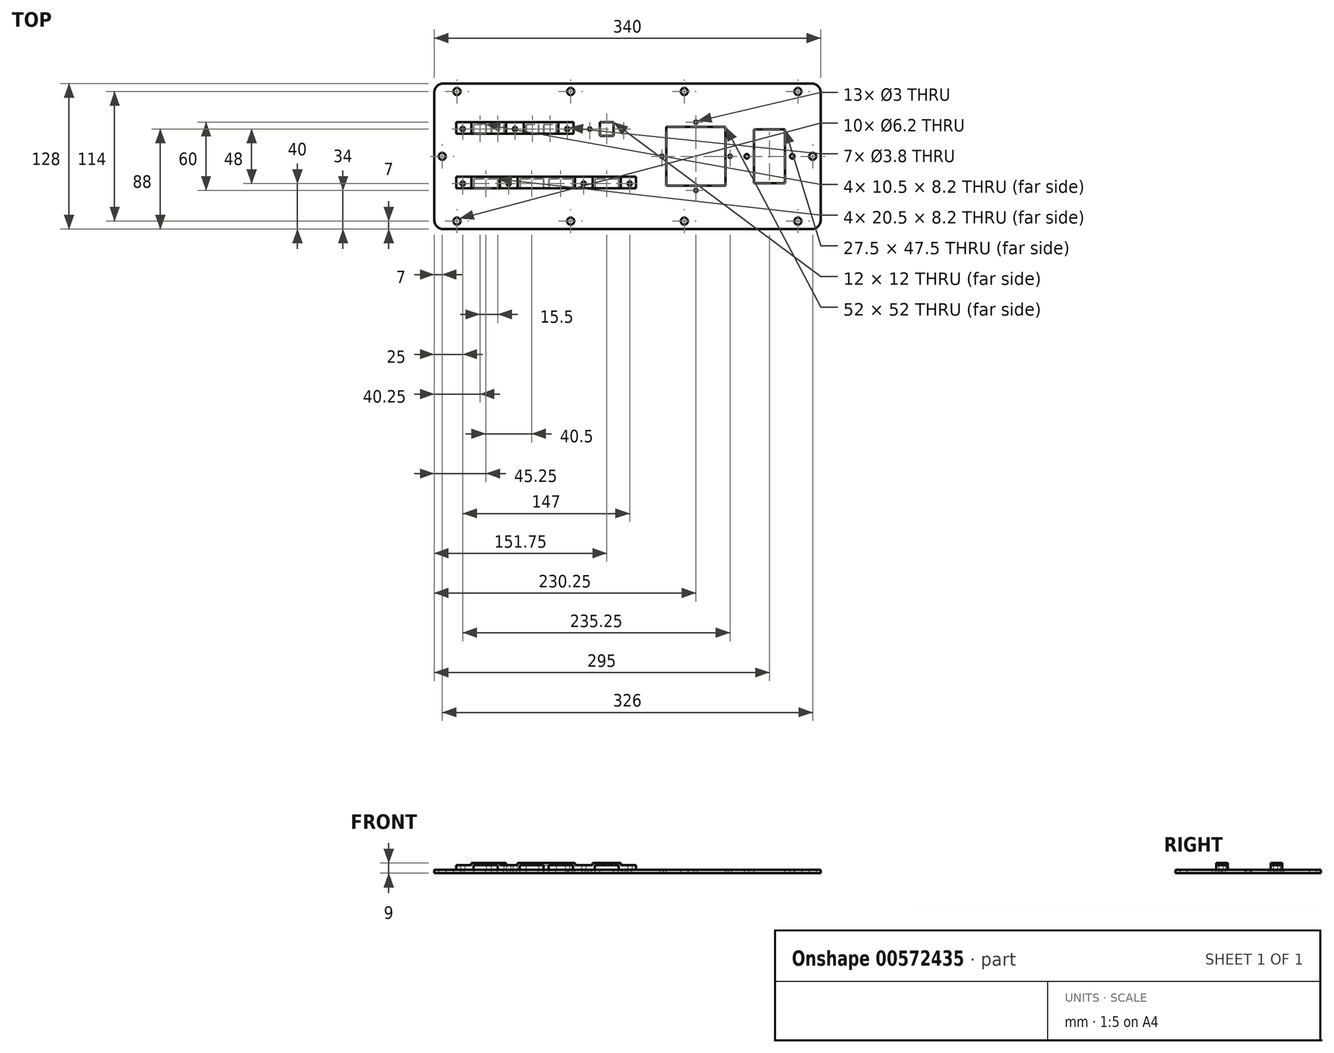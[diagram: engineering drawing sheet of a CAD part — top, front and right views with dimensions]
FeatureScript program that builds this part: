
annotation { "Feature Type Name" : "Feature", "Feature Type Description" : "" }
export const myFeature = defineFeature(function(context is Context, id is Id, definition is map)
    precondition{}
    {
        {
            var Q0;
            Q0=qCreatedBy(makeId("Top.planeOp"),FACE);
            var sketch = newSketch(context, id + "F0", { "sketchPlane" : qUnion([Q0])});
            skLineSegment(sketch, "E0.bottom", {"start": v(-170, 64) * mm, "end": v(170, 64) * mm});
            skLineSegment(sketch, "E0.top", {"start": v(-170, -64) * mm, "end": v(170, -64) * mm});
            skLineSegment(sketch, "E0.left", {"start": v(-170, 64) * mm, "end": v(-170, -64) * mm});
            skLineSegment(sketch, "E0.right", {"start": v(170, 64) * mm, "end": v(170, -64) * mm});
            skPoint(sketch, "E0.middle", {"position": v(0, 0) * mm});
            skLineSegment(sketch, "E1.0", {"start": v(-163, 57) * mm, "end": v(163, 57) * mm, "construction": true});
            skLineSegment(sketch, "E1.1", {"start": v(-163, 57) * mm, "end": v(-163, -57) * mm, "construction": true});
            skLineSegment(sketch, "E1.2", {"start": v(-163, -57) * mm, "end": v(163, -57) * mm, "construction": true});
            skLineSegment(sketch, "E1.3", {"start": v(163, 57) * mm, "end": v(163, -57) * mm, "construction": true});
            skCircle(sketch, "E2", {"center": v(-163, 0) * mm, "radius": 3.1 * mm});
            skCircle(sketch, "E3", {"center": v(-150, 57) * mm, "radius": 3.1 * mm});
            skCircle(sketch, "E4", {"center": v(-150, -57) * mm, "radius": 3.1 * mm});
            skCircle(sketch, "E5", {"center": v(-50, -57) * mm, "radius": 3.1 * mm});
            skCircle(sketch, "E6", {"center": v(-50, 57) * mm, "radius": 3.1 * mm});
            skLineSegment(sketch, "E7", {"start": v(0, 64) * mm, "end": v(0, -64) * mm, "construction": true});
            skCircle(sketch, "E8.MirrorC", {"center": v(50, -57) * mm, "radius": 3.1 * mm});
            skCircle(sketch, "E9.MirrorC", {"center": v(150, -57) * mm, "radius": 3.1 * mm});
            skCircle(sketch, "E10.MirrorC", {"center": v(163, 0) * mm, "radius": 3.1 * mm});
            skCircle(sketch, "E11.MirrorC", {"center": v(50, 57) * mm, "radius": 3.1 * mm});
            skCircle(sketch, "E12.MirrorC", {"center": v(150, 57) * mm, "radius": 3.1 * mm});
            skSolve(sketch);
        }
        {
            var Q0;
            Q0=makeQuery(id+"F0.imprint","IMPRINT",FACE,{"disambiguationData":[TD([[makeQuery(id+"F0.imprint","IMPRINT",EDGE,{"derivedFrom":sQuery(id+"F0.wireOp",EDGE,"E0.bottom")}),-1.0]])]});
            extrude(context, id + "F1", {"entities" : qUnion([Q0]), "depth" : 3 * mm, "offsetDistance" : 25 * mm});
        }
        {
            var Q0;
            Q0=makeQuery(id+"F1.opExtrude","CAP_FACE",FACE,{"disambiguationData":[OSD([sQuery(id+"F0.wireOp",EDGE,"E0.bottom"),sQuery(id+"F0.wireOp",EDGE,"E0.top"),sQuery(id+"F0.wireOp",EDGE,"E0.left"),sQuery(id+"F0.wireOp",EDGE,"E0.right"),sQuery(id+"F0.wireOp",EDGE,"E2"),sQuery(id+"F0.wireOp",EDGE,"E3"),sQuery(id+"F0.wireOp",EDGE,"E4"),sQuery(id+"F0.wireOp",EDGE,"E5"),sQuery(id+"F0.wireOp",EDGE,"E6"),sQuery(id+"F0.wireOp",EDGE,"E8.MirrorC"),sQuery(id+"F0.wireOp",EDGE,"E9.MirrorC"),sQuery(id+"F0.wireOp",EDGE,"E10.MirrorC"),sQuery(id+"F0.wireOp",EDGE,"E11.MirrorC"),sQuery(id+"F0.wireOp",EDGE,"E12.MirrorC")])],"isStart":false});
            var sketch = newSketch(context, id + "F2", { "sketchPlane" : qUnion([Q0])});
            skLineSegment(sketch, "E13.bottom", {"start": v(111.25, 23.75) * mm, "end": v(138.75, 23.75) * mm});
            skLineSegment(sketch, "E13.top", {"start": v(111.25, -23.75) * mm, "end": v(138.75, -23.75) * mm});
            skLineSegment(sketch, "E13.left", {"start": v(111.25, 23.75) * mm, "end": v(111.25, -23.75) * mm});
            skLineSegment(sketch, "E13.right", {"start": v(138.75, 23.75) * mm, "end": v(138.75, -23.75) * mm});
            skPoint(sketch, "E13.middle", {"position": v(125, 0) * mm});
            skLineSegment(sketch, "E14.bottom", {"start": v(34.25, 26) * mm, "end": v(86.25, 26) * mm});
            skLineSegment(sketch, "E14.top", {"start": v(34.25, -26) * mm, "end": v(86.25, -26) * mm});
            skLineSegment(sketch, "E14.left", {"start": v(34.25, 26) * mm, "end": v(34.25, -26) * mm});
            skLineSegment(sketch, "E14.right", {"start": v(86.25, 26) * mm, "end": v(86.25, -26) * mm});
            skPoint(sketch, "E14.middle", {"position": v(60.25, 0) * mm});
            skCircle(sketch, "E15", {"center": v(105, 0) * mm, "radius": 2 * mm});
            skPoint(sketch, "E15.centerSnap0", {"position": v(111.25, 0) * mm});
            skCircle(sketch, "E16", {"center": v(145, 0) * mm, "radius": 2 * mm});
            skPoint(sketch, "E16.centerSnap0", {"position": v(138.75, 0) * mm});
            skLineSegment(sketch, "E17", {"start": v(125, 23.75) * mm, "end": v(125, -23.75) * mm, "construction": true});
            skCircle(sketch, "E18", {"center": v(60.25, 30) * mm, "radius": 1.5 * mm});
            skCircle(sketch, "E19", {"center": v(60.25, -30) * mm, "radius": 1.5 * mm});
            skCircle(sketch, "E20", {"center": v(30.25, 0) * mm, "radius": 1.5 * mm});
            skCircle(sketch, "E21", {"center": v(90.25, 0) * mm, "radius": 1.5 * mm});
            skLineSegment(sketch, "E22", {"start": v(60.25, 26) * mm, "end": v(60.25, -26) * mm, "construction": true});
            skLineSegment(sketch, "E23", {"start": v(34.25, 0) * mm, "end": v(86.25, 0) * mm, "construction": true});
            skLineSegment(sketch, "E24.bottom", {"start": v(-135, -19.9) * mm, "end": v(-114.5, -19.9) * mm});
            skLineSegment(sketch, "E24.top", {"start": v(-135, -28.1) * mm, "end": v(-114.5, -28.1) * mm});
            skLineSegment(sketch, "E24.left", {"start": v(-135, -19.9) * mm, "end": v(-135, -28.1) * mm});
            skLineSegment(sketch, "E24.right", {"start": v(-114.5, -19.9) * mm, "end": v(-114.5, -28.1) * mm});
            skPoint(sketch, "E24.middle", {"position": v(-124.75, -24) * mm});
            skLineSegment(sketch, "E25.bottom", {"start": v(-94.5, -19.9) * mm, "end": v(-74, -19.9) * mm});
            skLineSegment(sketch, "E25.top", {"start": v(-94.5, -28.1) * mm, "end": v(-74, -28.1) * mm});
            skLineSegment(sketch, "E25.left", {"start": v(-94.5, -19.9) * mm, "end": v(-94.5, -28.1) * mm});
            skLineSegment(sketch, "E25.right", {"start": v(-74, -19.9) * mm, "end": v(-74, -28.1) * mm});
            skPoint(sketch, "E25.middle", {"position": v(-84.25, -24) * mm});
            skPoint(sketch, "E25.middle.positionSnap0", {"position": v(-114.5, -24) * mm});
            skPoint(sketch, "E25.centerSnap0", {"position": v(-114.5, -24) * mm});
            skLineSegment(sketch, "E26.bottom", {"start": v(-69, -19.9) * mm, "end": v(-48.5, -19.9) * mm});
            skLineSegment(sketch, "E26.top", {"start": v(-69, -28.1) * mm, "end": v(-48.5, -28.1) * mm});
            skLineSegment(sketch, "E26.left", {"start": v(-69, -19.9) * mm, "end": v(-69, -28.1) * mm});
            skLineSegment(sketch, "E26.right", {"start": v(-48.5, -19.9) * mm, "end": v(-48.5, -28.1) * mm});
            skPoint(sketch, "E26.middle", {"position": v(-58.75, -24) * mm});
            skLineSegment(sketch, "E27.bottom", {"start": v(-28.5, -19.9) * mm, "end": v(-8, -19.9) * mm});
            skLineSegment(sketch, "E27.top", {"start": v(-28.5, -28.1) * mm, "end": v(-8, -28.1) * mm});
            skLineSegment(sketch, "E27.left", {"start": v(-28.5, -19.9) * mm, "end": v(-28.5, -28.1) * mm});
            skLineSegment(sketch, "E27.right", {"start": v(-8, -19.9) * mm, "end": v(-8, -28.1) * mm});
            skPoint(sketch, "E27.middle", {"position": v(-18.25, -24) * mm});
            skCircle(sketch, "E28", {"center": v(-104.5, -24) * mm, "radius": 1.5 * mm});
            skPoint(sketch, "E28.centerSnap0", {"position": v(-94.5, -24) * mm});
            skCircle(sketch, "E29", {"center": v(-38.5, -24) * mm, "radius": 1.5 * mm});
            skPoint(sketch, "E29.centerSnap0", {"position": v(-48.5, -24) * mm});
            skCircle(sketch, "E30", {"center": v(2, -24) * mm, "radius": 1.5 * mm});
            skCircle(sketch, "E31", {"center": v(-145, -24) * mm, "radius": 1.5 * mm});
            skLineSegment(sketch, "E32.bottom", {"start": v(-124.5, 19.9) * mm, "end": v(-135, 19.9) * mm});
            skLineSegment(sketch, "E32.top", {"start": v(-124.5, 28.1) * mm, "end": v(-135, 28.1) * mm});
            skLineSegment(sketch, "E32.left", {"start": v(-124.5, 19.9) * mm, "end": v(-124.5, 28.1) * mm});
            skLineSegment(sketch, "E32.right", {"start": v(-135, 19.9) * mm, "end": v(-135, 28.1) * mm});
            skPoint(sketch, "E32.middle", {"position": v(-129.75, 24) * mm});
            skLineSegment(sketch, "E33.bottom", {"start": v(-119.5, 28.1) * mm, "end": v(-109, 28.1) * mm});
            skLineSegment(sketch, "E33.top", {"start": v(-119.5, 19.9) * mm, "end": v(-109, 19.9) * mm});
            skLineSegment(sketch, "E33.left", {"start": v(-119.5, 28.1) * mm, "end": v(-119.5, 19.9) * mm});
            skLineSegment(sketch, "E33.right", {"start": v(-109, 28.1) * mm, "end": v(-109, 19.9) * mm});
            skPoint(sketch, "E33.middle", {"position": v(-114.25, 24) * mm});
            skLineSegment(sketch, "E34.bottom", {"start": v(-89, 28.1) * mm, "end": v(-78.5, 28.1) * mm});
            skLineSegment(sketch, "E34.top", {"start": v(-89, 19.9) * mm, "end": v(-78.5, 19.9) * mm});
            skLineSegment(sketch, "E34.left", {"start": v(-89, 28.1) * mm, "end": v(-89, 19.9) * mm});
            skLineSegment(sketch, "E34.right", {"start": v(-78.5, 28.1) * mm, "end": v(-78.5, 19.9) * mm});
            skPoint(sketch, "E34.middle", {"position": v(-83.75, 24) * mm});
            skPoint(sketch, "E34.middle.positionSnap0", {"position": v(-109, 24) * mm});
            skPoint(sketch, "E34.centerSnap0", {"position": v(-109, 24) * mm});
            skLineSegment(sketch, "E35.bottom", {"start": v(-73.5, 28.1) * mm, "end": v(-63, 28.1) * mm});
            skLineSegment(sketch, "E35.top", {"start": v(-73.5, 19.9) * mm, "end": v(-63, 19.9) * mm});
            skLineSegment(sketch, "E35.left", {"start": v(-73.5, 28.1) * mm, "end": v(-73.5, 19.9) * mm});
            skLineSegment(sketch, "E35.right", {"start": v(-63, 28.1) * mm, "end": v(-63, 19.9) * mm});
            skPoint(sketch, "E35.middle", {"position": v(-68.25, 24) * mm});
            skCircle(sketch, "E36", {"center": v(-145, 24) * mm, "radius": 1.5 * mm});
            skPoint(sketch, "E36.centerSnap0", {"position": v(-135, 24) * mm});
            skCircle(sketch, "E37", {"center": v(-99, 24) * mm, "radius": 1.5 * mm});
            skPoint(sketch, "E37.centerSnap0", {"position": v(-124.5, 24) * mm});
            skCircle(sketch, "E38", {"center": v(-53, 24) * mm, "radius": 1.5 * mm});
            skPoint(sketch, "E38.centerSnap0", {"position": v(-63, 24) * mm});
            skLineSegment(sketch, "E39.bottom", {"start": v(-24.25, 30) * mm, "end": v(-12.25, 30) * mm});
            skLineSegment(sketch, "E39.top", {"start": v(-24.25, 18) * mm, "end": v(-12.25, 18) * mm});
            skLineSegment(sketch, "E39.left", {"start": v(-24.25, 30) * mm, "end": v(-24.25, 18) * mm});
            skLineSegment(sketch, "E39.right", {"start": v(-12.25, 30) * mm, "end": v(-12.25, 18) * mm});
            skPoint(sketch, "E39.middle", {"position": v(-18.25, 24) * mm});
            skCircle(sketch, "E40", {"center": v(-33.25, 24) * mm, "radius": 1.5 * mm});
            skPoint(sketch, "E40.centerSnap0", {"position": v(-24.25, 24) * mm});
            skCircle(sketch, "E41", {"center": v(-3.25, 24) * mm, "radius": 1.5 * mm});
            skPoint(sketch, "E41.centerSnap0", {"position": v(-12.25, 24) * mm});
            skLineSegment(sketch, "E42", {"start": v(-18.25, 30) * mm, "end": v(-18.25, 18) * mm, "construction": true});
            skSolve(sketch);
        }
        {
            var Q0;
            Q0 = qSketchRegion(id + "F2", true);
            extrude(context, id + "F3", {"entities" : qUnion([Q0]), "operationType" : NewBodyOperationType.REMOVE, "endBound" : BoundingType.THROUGH_ALL, "oppositeDirection" : true, "depth" : 25 * mm, "offsetDistance" : 25 * mm});
        }
        {
            var Q0;
            Q0=makeQuery(id+"F1.opExtrude","SWEPT_EDGE",EDGE,{"disambiguationData":[OSD([sQuery(id+"F0.wireOp",EDGE,"E0.top"),sQuery(id+"F0.wireOp",EDGE,"E0.right")])]});
            var Q1;
            Q1=makeQuery(id+"F1.opExtrude","SWEPT_EDGE",EDGE,{"disambiguationData":[OSD([sQuery(id+"F0.wireOp",EDGE,"E0.bottom"),sQuery(id+"F0.wireOp",EDGE,"E0.right")])]});
            var Q2;
            Q2=makeQuery(id+"F1.opExtrude","SWEPT_EDGE",EDGE,{"disambiguationData":[OSD([sQuery(id+"F0.wireOp",EDGE,"E0.top"),sQuery(id+"F0.wireOp",EDGE,"E0.left")])]});
            var Q3;
            Q3=makeQuery(id+"F1.opExtrude","SWEPT_EDGE",EDGE,{"disambiguationData":[OSD([sQuery(id+"F0.wireOp",EDGE,"E0.bottom"),sQuery(id+"F0.wireOp",EDGE,"E0.left")])]});
            fillet(context, id + "F4", {"entities" : qUnion([Q0, Q1, Q2, Q3]), "radius" : 8 * mm, "tangentPropagation" : true, "allowEdgeOverflow" : false});
        }
        {
            var Q0;
            Q0=makeQuery(id+"F1.opExtrude","CAP_FACE",FACE,{"disambiguationData":[OSD([sQuery(id+"F0.wireOp",EDGE,"E0.bottom"),sQuery(id+"F0.wireOp",EDGE,"E0.top"),sQuery(id+"F0.wireOp",EDGE,"E0.left"),sQuery(id+"F0.wireOp",EDGE,"E0.right"),sQuery(id+"F0.wireOp",EDGE,"E2"),sQuery(id+"F0.wireOp",EDGE,"E3"),sQuery(id+"F0.wireOp",EDGE,"E4"),sQuery(id+"F0.wireOp",EDGE,"E5"),sQuery(id+"F0.wireOp",EDGE,"E6"),sQuery(id+"F0.wireOp",EDGE,"E8.MirrorC"),sQuery(id+"F0.wireOp",EDGE,"E9.MirrorC"),sQuery(id+"F0.wireOp",EDGE,"E10.MirrorC"),sQuery(id+"F0.wireOp",EDGE,"E11.MirrorC"),sQuery(id+"F0.wireOp",EDGE,"E12.MirrorC")])],"isStart":false});
            var sketch = newSketch(context, id + "F5", { "sketchPlane" : qUnion([Q0])});
            skLineSegment(sketch, "E43.0", {"start": v(111.25, -23.75) * mm, "end": v(138.75, -23.75) * mm});
            skLineSegment(sketch, "E44.0", {"start": v(-162, 64) * mm, "end": v(162, 64) * mm});
            skLineSegment(sketch, "E44.1", {"start": v(-162, -64) * mm, "end": v(162, -64) * mm});
            skLineSegment(sketch, "E44.2", {"start": v(-170, 56) * mm, "end": v(-170, -56) * mm});
            skLineSegment(sketch, "E44.3", {"start": v(170, 56) * mm, "end": v(170, -56) * mm});
            skArc(sketch, "E45.0", {"start": v(170, 56) * mm, "mid": v(167.66, 61.66) * mm, "end": v(162, 64) * mm});
            skArc(sketch, "E45.1", {"start": v(-162, 64) * mm, "mid": v(-167.66, 61.66) * mm, "end": v(-170, 56) * mm});
            skArc(sketch, "E45.2", {"start": v(-170, -56) * mm, "mid": v(-167.66, -61.66) * mm, "end": v(-162, -64) * mm});
            skArc(sketch, "E45.3", {"start": v(162, -64) * mm, "mid": v(167.66, -61.66) * mm, "end": v(170, -56) * mm});
            skLineSegment(sketch, "E46.0", {"start": v(138.75, 23.75) * mm, "end": v(138.75, -23.75) * mm});
            skLineSegment(sketch, "E46.1", {"start": v(111.25, 23.75) * mm, "end": v(138.75, 23.75) * mm});
            skLineSegment(sketch, "E46.2", {"start": v(111.25, 23.75) * mm, "end": v(111.25, -23.75) * mm});
            skLineSegment(sketch, "E46.3", {"start": v(86.25, 26) * mm, "end": v(86.25, -26) * mm});
            skLineSegment(sketch, "E46.4", {"start": v(34.25, 26) * mm, "end": v(86.25, 26) * mm});
            skLineSegment(sketch, "E46.5", {"start": v(34.25, -26) * mm, "end": v(86.25, -26) * mm});
            skLineSegment(sketch, "E46.6", {"start": v(34.25, 26) * mm, "end": v(34.25, -26) * mm});
            skLineSegment(sketch, "E46.7", {"start": v(-28.5, -28.1) * mm, "end": v(-8, -28.1) * mm});
            skLineSegment(sketch, "E46.8", {"start": v(-8, -19.9) * mm, "end": v(-8, -28.1) * mm});
            skLineSegment(sketch, "E46.9", {"start": v(-28.5, -19.9) * mm, "end": v(-8, -19.9) * mm});
            skLineSegment(sketch, "E46.10", {"start": v(-28.5, -19.9) * mm, "end": v(-28.5, -28.1) * mm});
            skLineSegment(sketch, "E46.11", {"start": v(-24.25, 18) * mm, "end": v(-12.25, 18) * mm});
            skLineSegment(sketch, "E46.12", {"start": v(-24.25, 30) * mm, "end": v(-24.25, 18) * mm});
            skLineSegment(sketch, "E46.13", {"start": v(-24.25, 30) * mm, "end": v(-12.25, 30) * mm});
            skLineSegment(sketch, "E46.14", {"start": v(-12.25, 30) * mm, "end": v(-12.25, 18) * mm});
            skLineSegment(sketch, "E46.15", {"start": v(-124.5, 19.9) * mm, "end": v(-135, 19.9) * mm});
            skLineSegment(sketch, "E46.16", {"start": v(-124.5, 19.9) * mm, "end": v(-124.5, 28.1) * mm});
            skLineSegment(sketch, "E46.17", {"start": v(-135, 19.9) * mm, "end": v(-135, 28.1) * mm});
            skLineSegment(sketch, "E46.18", {"start": v(-124.5, 28.1) * mm, "end": v(-135, 28.1) * mm});
            skLineSegment(sketch, "E46.19", {"start": v(-119.5, 28.1) * mm, "end": v(-109, 28.1) * mm});
            skLineSegment(sketch, "E46.20", {"start": v(-119.5, 28.1) * mm, "end": v(-119.5, 19.9) * mm});
            skLineSegment(sketch, "E46.21", {"start": v(-119.5, 19.9) * mm, "end": v(-109, 19.9) * mm});
            skLineSegment(sketch, "E46.22", {"start": v(-109, 28.1) * mm, "end": v(-109, 19.9) * mm});
            skLineSegment(sketch, "E46.23", {"start": v(-89, 28.1) * mm, "end": v(-89, 19.9) * mm});
            skLineSegment(sketch, "E46.24", {"start": v(-89, 19.9) * mm, "end": v(-78.5, 19.9) * mm});
            skLineSegment(sketch, "E46.25", {"start": v(-78.5, 28.1) * mm, "end": v(-78.5, 19.9) * mm});
            skLineSegment(sketch, "E46.26", {"start": v(-89, 28.1) * mm, "end": v(-78.5, 28.1) * mm});
            skLineSegment(sketch, "E46.27", {"start": v(-73.5, 28.1) * mm, "end": v(-63, 28.1) * mm});
            skLineSegment(sketch, "E46.28", {"start": v(-73.5, 28.1) * mm, "end": v(-73.5, 19.9) * mm});
            skLineSegment(sketch, "E46.29", {"start": v(-73.5, 19.9) * mm, "end": v(-63, 19.9) * mm});
            skLineSegment(sketch, "E46.30", {"start": v(-63, 28.1) * mm, "end": v(-63, 19.9) * mm});
            skLineSegment(sketch, "E47.0", {"start": v(-135, -19.9) * mm, "end": v(-114.5, -19.9) * mm});
            skLineSegment(sketch, "E47.1", {"start": v(-135, -28.1) * mm, "end": v(-114.5, -28.1) * mm});
            skLineSegment(sketch, "E47.2", {"start": v(-135, -19.9) * mm, "end": v(-135, -28.1) * mm});
            skLineSegment(sketch, "E47.3", {"start": v(-114.5, -19.9) * mm, "end": v(-114.5, -28.1) * mm});
            skLineSegment(sketch, "E47.4", {"start": v(-94.5, -19.9) * mm, "end": v(-94.5, -28.1) * mm});
            skLineSegment(sketch, "E47.5", {"start": v(-94.5, -28.1) * mm, "end": v(-74, -28.1) * mm});
            skLineSegment(sketch, "E47.6", {"start": v(-94.5, -19.9) * mm, "end": v(-74, -19.9) * mm});
            skLineSegment(sketch, "E47.7", {"start": v(-74, -19.9) * mm, "end": v(-74, -28.1) * mm});
            skLineSegment(sketch, "E47.8", {"start": v(-69, -19.9) * mm, "end": v(-69, -28.1) * mm});
            skLineSegment(sketch, "E47.9", {"start": v(-69, -19.9) * mm, "end": v(-48.5, -19.9) * mm});
            skLineSegment(sketch, "E47.10", {"start": v(-69, -28.1) * mm, "end": v(-48.5, -28.1) * mm});
            skLineSegment(sketch, "E47.11", {"start": v(-48.5, -19.9) * mm, "end": v(-48.5, -28.1) * mm});
            skCircle(sketch, "E48.0", {"center": v(-150, -57) * mm, "radius": 3.1 * mm});
            skCircle(sketch, "E48.1", {"center": v(-163, 0) * mm, "radius": 3.1 * mm});
            skCircle(sketch, "E48.2", {"center": v(-150, 57) * mm, "radius": 3.1 * mm});
            skCircle(sketch, "E48.3", {"center": v(-50, 57) * mm, "radius": 3.1 * mm});
            skCircle(sketch, "E48.4", {"center": v(-50, -57) * mm, "radius": 3.1 * mm});
            skCircle(sketch, "E48.5", {"center": v(50, -57) * mm, "radius": 3.1 * mm});
            skCircle(sketch, "E48.6", {"center": v(50, 57) * mm, "radius": 3.1 * mm});
            skCircle(sketch, "E48.7", {"center": v(150, 57) * mm, "radius": 3.1 * mm});
            skCircle(sketch, "E48.8", {"center": v(163, 0) * mm, "radius": 3.1 * mm});
            skCircle(sketch, "E48.9", {"center": v(150, -57) * mm, "radius": 3.1 * mm});
            skCircle(sketch, "E49.0", {"center": v(145, 0) * mm, "radius": 2 * mm});
            skCircle(sketch, "E49.1", {"center": v(105, 0) * mm, "radius": 2 * mm});
            skCircle(sketch, "E49.2", {"center": v(90.25, 0) * mm, "radius": 1.5 * mm});
            skCircle(sketch, "E49.3", {"center": v(60.25, 30) * mm, "radius": 1.5 * mm});
            skCircle(sketch, "E49.4", {"center": v(30.25, 0) * mm, "radius": 1.5 * mm});
            skCircle(sketch, "E49.5", {"center": v(60.25, -30) * mm, "radius": 1.5 * mm});
            skCircle(sketch, "E50.0", {"center": v(2, -24) * mm, "radius": 1.5 * mm});
            skCircle(sketch, "E50.1", {"center": v(-3.25, 24) * mm, "radius": 1.5 * mm});
            skCircle(sketch, "E50.2", {"center": v(-33.25, 24) * mm, "radius": 1.5 * mm});
            skCircle(sketch, "E50.3", {"center": v(-38.5, -24) * mm, "radius": 1.5 * mm});
            skCircle(sketch, "E50.4", {"center": v(-53, 24) * mm, "radius": 1.5 * mm});
            skCircle(sketch, "E50.5", {"center": v(-99, 24) * mm, "radius": 1.5 * mm});
            skCircle(sketch, "E50.6", {"center": v(-104.5, -24) * mm, "radius": 1.5 * mm});
            skCircle(sketch, "E50.7", {"center": v(-145, -24) * mm, "radius": 1.5 * mm});
            skCircle(sketch, "E50.8", {"center": v(-145, 24) * mm, "radius": 1.5 * mm});
            skSolve(sketch);
        }
        {
            var Q0;
            Q0=makeQuery(id+"F5.imprint","IMPRINT",FACE,{"disambiguationData":[TD([[makeQuery(id+"F5.imprint","IMPRINT",EDGE,{"derivedFrom":sQuery(id+"F5.wireOp",EDGE,"E43.0")}),-1.0]])]});
            var sketch = newSketch(context, id + "F6", { "sketchPlane" : qUnion([Q0])});
            skLineSegment(sketch, "E51.bottom", {"start": v(-150.5, -17.9) * mm, "end": v(7.5, -17.9) * mm});
            skLineSegment(sketch, "E51.top", {"start": v(-150.5, -28.1) * mm, "end": v(7.5, -28.1) * mm});
            skLineSegment(sketch, "E51.left", {"start": v(-150.5, -17.9) * mm, "end": v(-150.5, -28.1) * mm});
            skLineSegment(sketch, "E51.right", {"start": v(7.5, -17.9) * mm, "end": v(7.5, -28.1) * mm});
            skLineSegment(sketch, "E52.0", {"start": v(-135.25, -19.9) * mm, "end": v(-135.25, -28.1) * mm});
            skLineSegment(sketch, "E53.0", {"start": v(-114.25, -19.9) * mm, "end": v(-114.25, -28.1) * mm});
            skLineSegment(sketch, "E54.0", {"start": v(-94.75, -19.9) * mm, "end": v(-94.75, -28.1) * mm});
            skLineSegment(sketch, "E55.0", {"start": v(-73.75, -19.9) * mm, "end": v(-73.75, -28.1) * mm});
            skLineSegment(sketch, "E56.0", {"start": v(-69.25, -19.9) * mm, "end": v(-69.25, -28.1) * mm});
            skLineSegment(sketch, "E57.0", {"start": v(-48.25, -19.9) * mm, "end": v(-48.25, -28.1) * mm});
            skLineSegment(sketch, "E58.0", {"start": v(-28.75, -19.9) * mm, "end": v(-28.75, -28.1) * mm});
            skLineSegment(sketch, "E59.0", {"start": v(-7.75, -19.9) * mm, "end": v(-7.75, -28.1) * mm});
            skLineSegment(sketch, "E60.0", {"start": v(-135, -19.9) * mm, "end": v(-114.5, -19.9) * mm});
            skLineSegment(sketch, "E60.1", {"start": v(-94.5, -19.9) * mm, "end": v(-74, -19.9) * mm});
            skLineSegment(sketch, "E60.2", {"start": v(-69, -19.9) * mm, "end": v(-48.5, -19.9) * mm});
            skLineSegment(sketch, "E60.3", {"start": v(-28.5, -19.9) * mm, "end": v(-8, -19.9) * mm});
            skCircle(sketch, "E61.0", {"center": v(-145, -24) * mm, "radius": 1.5 * mm, "construction": true});
            skCircle(sketch, "E61.1", {"center": v(-104.5, -24) * mm, "radius": 1.5 * mm, "construction": true});
            skCircle(sketch, "E61.2", {"center": v(-38.5, -24) * mm, "radius": 1.5 * mm, "construction": true});
            skCircle(sketch, "E61.3", {"center": v(2, -24) * mm, "radius": 1.5 * mm, "construction": true});
            skLineSegment(sketch, "E62", {"start": v(-7.75, -19.9) * mm, "end": v(-8, -19.9) * mm});
            skLineSegment(sketch, "E63", {"start": v(-28.5, -19.9) * mm, "end": v(-28.75, -19.9) * mm});
            skLineSegment(sketch, "E64", {"start": v(-48.25, -19.9) * mm, "end": v(-48.5, -19.9) * mm});
            skLineSegment(sketch, "E65", {"start": v(-69, -19.9) * mm, "end": v(-69.25, -19.9) * mm});
            skLineSegment(sketch, "E66", {"start": v(-73.75, -19.9) * mm, "end": v(-74, -19.9) * mm});
            skLineSegment(sketch, "E67", {"start": v(-94.5, -19.9) * mm, "end": v(-94.75, -19.9) * mm});
            skLineSegment(sketch, "E68", {"start": v(-114.25, -19.9) * mm, "end": v(-114.5, -19.9) * mm});
            skLineSegment(sketch, "E69", {"start": v(-135, -19.9) * mm, "end": v(-135.25, -19.9) * mm});
            skCircle(sketch, "E70.0", {"center": v(-145, -24) * mm, "radius": 1.9 * mm});
            skCircle(sketch, "E71.0", {"center": v(-104.5, -24) * mm, "radius": 1.9 * mm});
            skCircle(sketch, "E72.0", {"center": v(-38.5, -24) * mm, "radius": 1.9 * mm});
            skCircle(sketch, "E73.0", {"center": v(2, -24) * mm, "radius": 1.9 * mm});
            skSolve(sketch);
        }
        {
            var Q0;
            Q0=makeQuery(id+"F6.imprint","IMPRINT",FACE,{"disambiguationData":[TD([[makeQuery(id+"F6.imprint","IMPRINT",EDGE,{"derivedFrom":sQuery(id+"F6.wireOp",EDGE,"E51.bottom")}),-1.0]])]});
            extrude(context, id + "F7", {"entities" : qUnion([Q0]), "depth" : 4 * mm, "offsetDistance" : 25 * mm});
        }
        {
            var Q0;
            Q0=makeQuery(id+"F7.opExtrude","CAP_FACE",FACE,{"disambiguationData":[OSD([sQuery(id+"F5.wireOp",EDGE,"E46.8"),sQuery(id+"F5.wireOp",EDGE,"E46.10"),sQuery(id+"F5.wireOp",EDGE,"E47.2"),sQuery(id+"F5.wireOp",EDGE,"E47.3"),sQuery(id+"F5.wireOp",EDGE,"E47.4"),sQuery(id+"F5.wireOp",EDGE,"E47.7"),sQuery(id+"F5.wireOp",EDGE,"E47.8"),sQuery(id+"F5.wireOp",EDGE,"E47.11"),sQuery(id+"F6.wireOp",EDGE,"E51.bottom"),sQuery(id+"F6.wireOp",EDGE,"E51.top"),sQuery(id+"F6.wireOp",EDGE,"E51.left"),sQuery(id+"F6.wireOp",EDGE,"E51.right"),sQuery(id+"F6.wireOp",EDGE,"E60.0"),sQuery(id+"F6.wireOp",EDGE,"E60.1"),sQuery(id+"F6.wireOp",EDGE,"E60.2"),sQuery(id+"F6.wireOp",EDGE,"E60.3"),sQuery(id+"F6.wireOp",EDGE,"E61.0"),sQuery(id+"F6.wireOp",EDGE,"E61.1"),sQuery(id+"F6.wireOp",EDGE,"E61.2"),sQuery(id+"F6.wireOp",EDGE,"E61.3")])],"isStart":false});
            var sketch = newSketch(context, id + "F8", { "sketchPlane" : qUnion([Q0])});
            skLineSegment(sketch, "E74.bottom", {"start": v(-137.25, -17.9) * mm, "end": v(-112.25, -17.9) * mm});
            skLineSegment(sketch, "E74.top", {"start": v(-137.25, -28.1) * mm, "end": v(-112.25, -28.1) * mm});
            skLineSegment(sketch, "E74.left", {"start": v(-137.25, -17.9) * mm, "end": v(-137.25, -28.1) * mm});
            skLineSegment(sketch, "E74.right", {"start": v(-112.25, -17.9) * mm, "end": v(-112.25, -28.1) * mm});
            skLineSegment(sketch, "E75.bottom", {"start": v(-96.75, -17.9) * mm, "end": v(-46.25, -17.9) * mm});
            skLineSegment(sketch, "E75.top", {"start": v(-96.75, -28.1) * mm, "end": v(-46.25, -28.1) * mm});
            skLineSegment(sketch, "E75.left", {"start": v(-96.75, -17.9) * mm, "end": v(-96.75, -28.1) * mm});
            skLineSegment(sketch, "E75.right", {"start": v(-46.25, -17.9) * mm, "end": v(-46.25, -28.1) * mm});
            skLineSegment(sketch, "E76.bottom", {"start": v(-30.75, -17.9) * mm, "end": v(-5.75, -17.9) * mm});
            skLineSegment(sketch, "E76.top", {"start": v(-30.75, -28.1) * mm, "end": v(-5.75, -28.1) * mm});
            skLineSegment(sketch, "E76.left", {"start": v(-30.75, -17.9) * mm, "end": v(-30.75, -28.1) * mm});
            skLineSegment(sketch, "E76.right", {"start": v(-5.75, -17.9) * mm, "end": v(-5.75, -28.1) * mm});
            skSolve(sketch);
        }
        {
            var Q0;
            Q0=makeQuery(id+"F8.imprint","IMPRINT",FACE,{"disambiguationData":[TD([[makeQuery(id+"F8.imprint","IMPRINT",EDGE,{"derivedFrom":sQuery(id+"F8.wireOp",EDGE,"E74.bottom")}),-1.0]])]});
            var Q1;
            Q1=makeQuery(id+"F8.imprint","IMPRINT",FACE,{"disambiguationData":[TD([[makeQuery(id+"F8.imprint","IMPRINT",EDGE,{"derivedFrom":makeQuery(id+"F7.opExtrude","CAP_EDGE",EDGE,{"disambiguationData":[OSD([sQuery(id+"F6.wireOp",EDGE,"E60.0")])],"isStart":false})}),-1.0]])]});
            var Q2;
            Q2=makeQuery(id+"F8.imprint","IMPRINT",FACE,{"disambiguationData":[TD([[makeQuery(id+"F8.imprint","IMPRINT",EDGE,{"derivedFrom":sQuery(id+"F8.wireOp",EDGE,"E75.bottom")}),-1.0]])]});
            var Q3;
            Q3=makeQuery(id+"F8.imprint","IMPRINT",FACE,{"disambiguationData":[TD([[makeQuery(id+"F8.imprint","IMPRINT",EDGE,{"derivedFrom":makeQuery(id+"F7.opExtrude","CAP_EDGE",EDGE,{"disambiguationData":[OSD([sQuery(id+"F6.wireOp",EDGE,"E60.1")])],"isStart":false})}),-1.0]])]});
            var Q4;
            Q4=makeQuery(id+"F8.imprint","IMPRINT",FACE,{"disambiguationData":[TD([[makeQuery(id+"F8.imprint","IMPRINT",EDGE,{"derivedFrom":makeQuery(id+"F7.opExtrude","CAP_EDGE",EDGE,{"disambiguationData":[OSD([sQuery(id+"F6.wireOp",EDGE,"E60.2")])],"isStart":false})}),-1.0]])]});
            var Q5;
            Q5=makeQuery(id+"F8.imprint","IMPRINT",FACE,{"disambiguationData":[TD([[makeQuery(id+"F8.imprint","IMPRINT",EDGE,{"derivedFrom":sQuery(id+"F8.wireOp",EDGE,"E76.bottom")}),-1.0]])]});
            var Q6;
            Q6=makeQuery(id+"F8.imprint","IMPRINT",FACE,{"disambiguationData":[TD([[makeQuery(id+"F8.imprint","IMPRINT",EDGE,{"derivedFrom":makeQuery(id+"F7.opExtrude","CAP_EDGE",EDGE,{"disambiguationData":[OSD([sQuery(id+"F6.wireOp",EDGE,"E60.3")])],"isStart":false})}),-1.0]])]});
            var Q7;
            {var subQ1=makeQuery(id+"F7.opExtrude","CAP_EDGE",EDGE,{"disambiguationData":[OSD([sQuery(id+"F6.wireOp",EDGE,"E52.0")])],"isStart":false});Q7=makeQuery(id+"F8.imprint","IMPRINT",FACE,{"disambiguationData":[TD([[makeQuery(id+"F8.imprint","IMPRINT",EDGE,{"derivedFrom":subQ1}),1.0]])]});}
            var Q8;
            {var subQ1=makeQuery(id+"F7.opExtrude","CAP_EDGE",EDGE,{"disambiguationData":[OSD([sQuery(id+"F6.wireOp",EDGE,"E54.0")])],"isStart":false});Q8=makeQuery(id+"F8.imprint","IMPRINT",FACE,{"disambiguationData":[TD([[makeQuery(id+"F8.imprint","IMPRINT",EDGE,{"derivedFrom":subQ1}),1.0]])]});}
            var Q9;
            {var subQ1=makeQuery(id+"F7.opExtrude","CAP_EDGE",EDGE,{"disambiguationData":[OSD([sQuery(id+"F6.wireOp",EDGE,"E56.0")])],"isStart":false});Q9=makeQuery(id+"F8.imprint","IMPRINT",FACE,{"disambiguationData":[TD([[makeQuery(id+"F8.imprint","IMPRINT",EDGE,{"derivedFrom":subQ1}),1.0]])]});}
            var Q10;
            {var subQ1=makeQuery(id+"F7.opExtrude","CAP_EDGE",EDGE,{"disambiguationData":[OSD([sQuery(id+"F6.wireOp",EDGE,"E58.0")])],"isStart":false});Q10=makeQuery(id+"F8.imprint","IMPRINT",FACE,{"disambiguationData":[TD([[makeQuery(id+"F8.imprint","IMPRINT",EDGE,{"derivedFrom":subQ1}),1.0]])]});}
            extrude(context, id + "F9", {"entities" : qUnion([Q0, Q1, Q2, Q3, Q4, Q5, Q6, Q7, Q8, Q9, Q10]), "operationType" : NewBodyOperationType.ADD, "depth" : 2 * mm, "offsetDistance" : 25 * mm});
        }
        {
            var Q0;
            Q0=makeQuery(id+"F1.opExtrude","CAP_FACE",FACE,{"disambiguationData":[OSD([sQuery(id+"F0.wireOp",EDGE,"E0.bottom"),sQuery(id+"F0.wireOp",EDGE,"E0.top"),sQuery(id+"F0.wireOp",EDGE,"E0.left"),sQuery(id+"F0.wireOp",EDGE,"E0.right"),sQuery(id+"F0.wireOp",EDGE,"E2"),sQuery(id+"F0.wireOp",EDGE,"E3"),sQuery(id+"F0.wireOp",EDGE,"E4"),sQuery(id+"F0.wireOp",EDGE,"E5"),sQuery(id+"F0.wireOp",EDGE,"E6"),sQuery(id+"F0.wireOp",EDGE,"E8.MirrorC"),sQuery(id+"F0.wireOp",EDGE,"E9.MirrorC"),sQuery(id+"F0.wireOp",EDGE,"E10.MirrorC"),sQuery(id+"F0.wireOp",EDGE,"E11.MirrorC"),sQuery(id+"F0.wireOp",EDGE,"E12.MirrorC")])],"isStart":false});
            var sketch = newSketch(context, id + "F10", { "sketchPlane" : qUnion([Q0])});
            skLineSegment(sketch, "E77.bottom", {"start": v(-150.5, 30.1) * mm, "end": v(-47.5, 30.1) * mm});
            skLineSegment(sketch, "E77.top", {"start": v(-150.5, 19.9) * mm, "end": v(-47.5, 19.9) * mm});
            skLineSegment(sketch, "E77.left", {"start": v(-150.5, 30.1) * mm, "end": v(-150.5, 19.9) * mm});
            skLineSegment(sketch, "E77.right", {"start": v(-47.5, 30.1) * mm, "end": v(-47.5, 19.9) * mm});
            skLineSegment(sketch, "E78", {"start": v(-135.23, 19.9) * mm, "end": v(-135.23, 28.1) * mm});
            skLineSegment(sketch, "E79", {"start": v(-135.23, 28.1) * mm, "end": v(-124.28, 28.1) * mm});
            skLineSegment(sketch, "E80", {"start": v(-124.28, 28.1) * mm, "end": v(-124.28, 19.9) * mm});
            skLineSegment(sketch, "E81", {"start": v(-124.28, 19.9) * mm, "end": v(-119.73, 19.9) * mm});
            skLineSegment(sketch, "E82", {"start": v(-119.73, 19.9) * mm, "end": v(-119.73, 28.1) * mm});
            skLineSegment(sketch, "E83", {"start": v(-119.73, 28.1) * mm, "end": v(-108.78, 28.1) * mm});
            skLineSegment(sketch, "E84", {"start": v(-108.78, 28.1) * mm, "end": v(-108.78, 19.9) * mm});
            skLineSegment(sketch, "E85", {"start": v(-89.23, 19.9) * mm, "end": v(-89.23, 28.1) * mm});
            skLineSegment(sketch, "E86", {"start": v(-89.23, 28.1) * mm, "end": v(-78.28, 28.1) * mm});
            skLineSegment(sketch, "E87", {"start": v(-78.28, 28.1) * mm, "end": v(-78.28, 19.9) * mm});
            skLineSegment(sketch, "E88", {"start": v(-73.73, 19.9) * mm, "end": v(-73.73, 28.1) * mm});
            skLineSegment(sketch, "E89", {"start": v(-73.73, 28.1) * mm, "end": v(-62.78, 28.1) * mm});
            skLineSegment(sketch, "E90", {"start": v(-62.78, 28.1) * mm, "end": v(-62.78, 19.9) * mm});
            skCircle(sketch, "E91.0", {"center": v(-145, 24) * mm, "radius": 1.9 * mm});
            skCircle(sketch, "E92.0", {"center": v(-99, 24) * mm, "radius": 1.9 * mm});
            skCircle(sketch, "E93.0", {"center": v(-53, 24) * mm, "radius": 1.9 * mm});
            skSolve(sketch);
        }
        {
            var Q0;
            Q0=makeQuery(id+"F10.imprint","IMPRINT",FACE,{"disambiguationData":[TD([[makeQuery(id+"F10.imprint","IMPRINT",EDGE,{"derivedFrom":sQuery(id+"F10.wireOp",EDGE,"E77.bottom")}),-1.0]])]});
            extrude(context, id + "F11", {"entities" : qUnion([Q0]), "depth" : 4 * mm, "offsetDistance" : 25 * mm});
        }
        {
            var Q0;
            Q0=makeQuery(id+"F11.opExtrude","CAP_FACE",FACE,{"disambiguationData":[OSD([sQuery(id+"F10.wireOp",EDGE,"E77.bottom"),sQuery(id+"F10.wireOp",EDGE,"E77.top"),sQuery(id+"F10.wireOp",EDGE,"E77.left"),sQuery(id+"F10.wireOp",EDGE,"E77.right"),sQuery(id+"F10.wireOp",EDGE,"E78"),sQuery(id+"F10.wireOp",EDGE,"E79"),sQuery(id+"F10.wireOp",EDGE,"E80"),sQuery(id+"F10.wireOp",EDGE,"E81"),sQuery(id+"F10.wireOp",EDGE,"E82"),sQuery(id+"F10.wireOp",EDGE,"E83"),sQuery(id+"F10.wireOp",EDGE,"E84"),sQuery(id+"F10.wireOp",EDGE,"E85"),sQuery(id+"F10.wireOp",EDGE,"E86"),sQuery(id+"F10.wireOp",EDGE,"E87"),sQuery(id+"F10.wireOp",EDGE,"E88"),sQuery(id+"F10.wireOp",EDGE,"E89"),sQuery(id+"F10.wireOp",EDGE,"E90"),sQuery(id+"F10.wireOp",EDGE,"E91.0"),sQuery(id+"F10.wireOp",EDGE,"E92.0"),sQuery(id+"F10.wireOp",EDGE,"E93.0")])],"isStart":false});
            var sketch = newSketch(context, id + "F12", { "sketchPlane" : qUnion([Q0])});
            skLineSegment(sketch, "E94", {"start": v(-137.23, 30.1) * mm, "end": v(-137.23, 19.9) * mm});
            skLineSegment(sketch, "E95", {"start": v(-106.78, 30.1) * mm, "end": v(-106.78, 19.9) * mm});
            skLineSegment(sketch, "E96", {"start": v(-91.23, 30.1) * mm, "end": v(-91.23, 19.9) * mm});
            skLineSegment(sketch, "E97", {"start": v(-60.78, 30.1) * mm, "end": v(-60.78, 19.9) * mm});
            skLineSegment(sketch, "E98", {"start": v(-137.23, 19.9) * mm, "end": v(-106.78, 19.9) * mm});
            skLineSegment(sketch, "E99", {"start": v(-91.23, 19.9) * mm, "end": v(-60.78, 19.9) * mm});
            skLineSegment(sketch, "E100", {"start": v(-60.78, 30.1) * mm, "end": v(-91.23, 30.1) * mm});
            skLineSegment(sketch, "E101", {"start": v(-137.23, 30.1) * mm, "end": v(-106.78, 30.1) * mm});
            skSolve(sketch);
        }
        {
            var Q0;
            {var subQ6=sQuery(id+"F12.wireOp",EDGE,"E94");Q0=makeQuery(id+"F12.imprint","IMPRINT",FACE,{"disambiguationData":[TD([[makeQuery(id+"F12.imprint","IMPRINT",EDGE,{"derivedFrom":subQ6}),1.0]])]});}
            var Q1;
            {var subQ1=makeQuery(id+"F11.opExtrude","CAP_EDGE",EDGE,{"disambiguationData":[OSD([sQuery(id+"F10.wireOp",EDGE,"E78")])],"isStart":false});Q1=makeQuery(id+"F12.imprint","IMPRINT",FACE,{"disambiguationData":[TD([[makeQuery(id+"F12.imprint","IMPRINT",EDGE,{"derivedFrom":subQ1}),-1.0]])]});}
            var Q2;
            {var subQ1=makeQuery(id+"F11.opExtrude","CAP_EDGE",EDGE,{"disambiguationData":[OSD([sQuery(id+"F10.wireOp",EDGE,"E82")])],"isStart":false});Q2=makeQuery(id+"F12.imprint","IMPRINT",FACE,{"disambiguationData":[TD([[makeQuery(id+"F12.imprint","IMPRINT",EDGE,{"derivedFrom":subQ1}),-1.0]])]});}
            var Q3;
            {var subQ9=sQuery(id+"F12.wireOp",EDGE,"E96");Q3=makeQuery(id+"F12.imprint","IMPRINT",FACE,{"disambiguationData":[TD([[makeQuery(id+"F12.imprint","IMPRINT",EDGE,{"derivedFrom":subQ9}),1.0]])]});}
            var Q4;
            {var subQ1=makeQuery(id+"F11.opExtrude","CAP_EDGE",EDGE,{"disambiguationData":[OSD([sQuery(id+"F10.wireOp",EDGE,"E85")])],"isStart":false});Q4=makeQuery(id+"F12.imprint","IMPRINT",FACE,{"disambiguationData":[TD([[makeQuery(id+"F12.imprint","IMPRINT",EDGE,{"derivedFrom":subQ1}),-1.0]])]});}
            var Q5;
            {var subQ1=makeQuery(id+"F11.opExtrude","CAP_EDGE",EDGE,{"disambiguationData":[OSD([sQuery(id+"F10.wireOp",EDGE,"E88")])],"isStart":false});Q5=makeQuery(id+"F12.imprint","IMPRINT",FACE,{"disambiguationData":[TD([[makeQuery(id+"F12.imprint","IMPRINT",EDGE,{"derivedFrom":subQ1}),-1.0]])]});}
            extrude(context, id + "F13", {"entities" : qUnion([Q0, Q1, Q2, Q3, Q4, Q5]), "operationType" : NewBodyOperationType.ADD, "depth" : 2 * mm, "offsetDistance" : 25 * mm});
        }
    });
